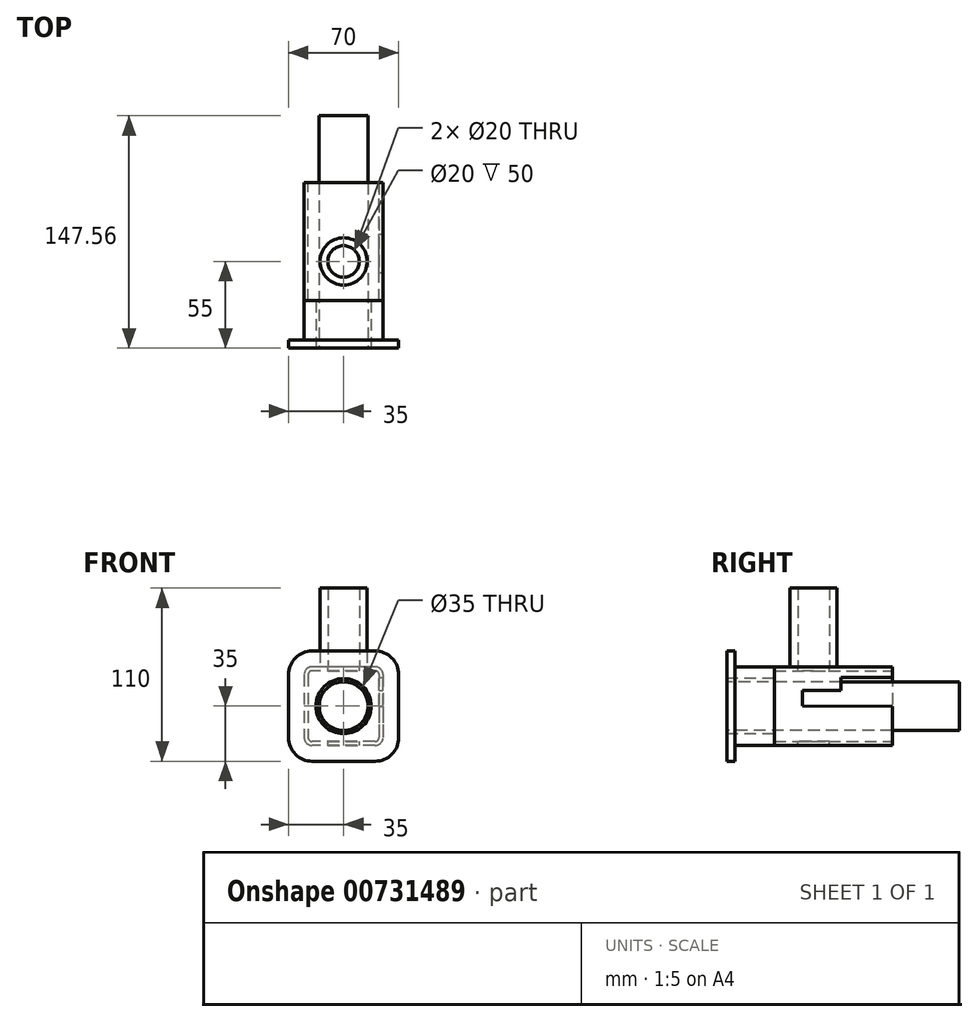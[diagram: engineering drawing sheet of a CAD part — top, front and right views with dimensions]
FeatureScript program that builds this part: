
annotation { "Feature Type Name" : "Feature", "Feature Type Description" : "" }
export const myFeature = defineFeature(function(context is Context, id is Id, definition is map)
    precondition{}
    {
        {
            var Q0;
            Q0=qCreatedBy(makeId("Front.planeOp"),FACE);
            var sketch = newSketch(context, id + "F0", { "sketchPlane" : qUnion([Q0])});
            skLineSegment(sketch, "E0.bottom", {"start": v(25, 25) * mm, "end": v(-25, 25) * mm});
            skLineSegment(sketch, "E0.top", {"start": v(25, -25) * mm, "end": v(-25, -25) * mm});
            skLineSegment(sketch, "E0.left", {"start": v(25, 25) * mm, "end": v(25, -25) * mm});
            skLineSegment(sketch, "E0.right", {"start": v(-25, 25) * mm, "end": v(-25, -25) * mm});
            skPoint(sketch, "E0.middle", {"position": v(0, 0) * mm});
            skSolve(sketch);
        }
        {
            var Q0;
            Q0 = qSketchRegion(id + "F0", true);
            extrude(context, id + "F1", {"entities" : qUnion([Q0]), "depth" : 75 * mm, "offsetDistance" : 25 * mm});
        }
        {
            var Q0;
            Q0=makeQuery(id+"F1.opExtrude","SWEPT_EDGE",EDGE,{"disambiguationData":[OSD([sQuery(id+"F0.wireOp",EDGE,"E0.top"),sQuery(id+"F0.wireOp",EDGE,"E0.right")])]});
            var Q1;
            Q1=makeQuery(id+"F1.opExtrude","SWEPT_EDGE",EDGE,{"disambiguationData":[OSD([sQuery(id+"F0.wireOp",EDGE,"E0.top"),sQuery(id+"F0.wireOp",EDGE,"E0.left")])]});
            var Q2;
            Q2=makeQuery(id+"F1.opExtrude","SWEPT_EDGE",EDGE,{"disambiguationData":[OSD([sQuery(id+"F0.wireOp",EDGE,"E0.bottom"),sQuery(id+"F0.wireOp",EDGE,"E0.right")])]});
            var Q3;
            Q3=makeQuery(id+"F1.opExtrude","SWEPT_EDGE",EDGE,{"disambiguationData":[OSD([sQuery(id+"F0.wireOp",EDGE,"E0.bottom"),sQuery(id+"F0.wireOp",EDGE,"E0.left")])]});
            fillet(context, id + "F2", {"entities" : qUnion([Q0, Q1, Q2, Q3]), "radius" : 5 * mm, "tangentPropagation" : true, "allowEdgeOverflow" : false});
        }
        {
            var Q0;
            Q0=makeQuery(id+"F1.opExtrude","CAP_FACE",FACE,{"disambiguationData":[OSD([sQuery(id+"F0.wireOp",EDGE,"E0.bottom"),sQuery(id+"F0.wireOp",EDGE,"E0.top"),sQuery(id+"F0.wireOp",EDGE,"E0.left"),sQuery(id+"F0.wireOp",EDGE,"E0.right")])],"isStart":false});
            var Q1;
            Q1=makeQuery(id+"F1.opExtrude","CAP_FACE",FACE,{"disambiguationData":[OSD([sQuery(id+"F0.wireOp",EDGE,"E0.bottom"),sQuery(id+"F0.wireOp",EDGE,"E0.top"),sQuery(id+"F0.wireOp",EDGE,"E0.left"),sQuery(id+"F0.wireOp",EDGE,"E0.right")])],"isStart":true});
            shell(context, id + "F3", {"entities" : qUnion([Q0, Q1]), "thickness" : 2.5 * mm});
        }
        {
            var Q0;
            Q0=makeQuery(id+"F1.opExtrude","SWEPT_FACE",FACE,{"disambiguationData":[OSD([sQuery(id+"F0.wireOp",EDGE,"E0.bottom")])]});
            var sketch = newSketch(context, id + "F4", { "sketchPlane" : qUnion([Q0])});
            skCircle(sketch, "E1", {"center": v(0, -50) * mm, "radius": 10 * mm});
            skSolve(sketch);
        }
        {
            var Q0;
            Q0 = qSketchRegion(id + "F4", true);
            extrude(context, id + "F5", {"entities" : qUnion([Q0]), "operationType" : NewBodyOperationType.REMOVE, "endBound" : BoundingType.THROUGH_ALL, "oppositeDirection" : true, "depth" : 41.42 * mm, "offsetDistance" : 25 * mm});
        }
        {
            var Q0;
            Q0=makeQuery(id+"F1.opExtrude","SWEPT_FACE",FACE,{"disambiguationData":[OSD([sQuery(id+"F0.wireOp",EDGE,"E0.left")])]});
            var sketch = newSketch(context, id + "F6", { "sketchPlane" : qUnion([Q0])});
            skLineSegment(sketch, "E2", {"start": v(-57, 0) * mm, "end": v(-57, 10) * mm});
            skLineSegment(sketch, "E3", {"start": v(-57, 10) * mm, "end": v(-32.57, 10) * mm});
            skLineSegment(sketch, "E4", {"start": v(-32.57, 10) * mm, "end": v(-32.57, 18.28) * mm});
            skLineSegment(sketch, "E5", {"start": v(0, 18.28) * mm, "end": v(0, -0.12) * mm});
            skLineSegment(sketch, "E6", {"start": v(0, 18.28) * mm, "end": v(-32.57, 18.28) * mm});
            skLineSegment(sketch, "E7", {"start": v(0, -0.12) * mm, "end": v(-57, 0) * mm});
            skSolve(sketch);
        }
        {
            var Q0;
            Q0=makeQuery(id+"F6.imprint","IMPRINT",FACE,{"disambiguationData":[TD([[makeQuery(id+"F6.imprint","IMPRINT",EDGE,{"derivedFrom":sQuery(id+"F6.wireOp",EDGE,"E2")}),-1.0]])]});
            extrude(context, id + "F7", {"entities" : qUnion([Q0]), "operationType" : NewBodyOperationType.REMOVE, "oppositeDirection" : true, "depth" : 3 * mm, "offsetDistance" : 25 * mm});
        }
        {
            var Q0;
            Q0=makeQuery(id+"F1.opExtrude","CAP_FACE",FACE,{"disambiguationData":[OSD([sQuery(id+"F0.wireOp",EDGE,"E0.bottom"),sQuery(id+"F0.wireOp",EDGE,"E0.top"),sQuery(id+"F0.wireOp",EDGE,"E0.left"),sQuery(id+"F0.wireOp",EDGE,"E0.right")])],"isStart":false});
            var sketch = newSketch(context, id + "F8", { "sketchPlane" : qUnion([Q0])});
            skLineSegment(sketch, "E8.0", {"start": v(20, 25) * mm, "end": v(-20, 25) * mm});
            skArc(sketch, "E9.0", {"start": v(25, 20) * mm, "mid": v(23.54, 23.54) * mm, "end": v(20, 25) * mm});
            skLineSegment(sketch, "E10.0", {"start": v(25, 20) * mm, "end": v(25, -20) * mm});
            skArc(sketch, "E11.0", {"start": v(20, -25) * mm, "mid": v(23.54, -23.54) * mm, "end": v(25, -20) * mm});
            skLineSegment(sketch, "E12.0", {"start": v(20, -25) * mm, "end": v(-20, -25) * mm});
            skArc(sketch, "E13.0", {"start": v(-25, -20) * mm, "mid": v(-23.54, -23.54) * mm, "end": v(-20, -25) * mm});
            skLineSegment(sketch, "E14.0", {"start": v(-25, 20) * mm, "end": v(-25, -20) * mm});
            skArc(sketch, "E15.0", {"start": v(-20, 25) * mm, "mid": v(-23.54, 23.54) * mm, "end": v(-25, 20) * mm});
            skSolve(sketch);
        }
        {
            var Q0;
            Q0 = qSketchRegion(id + "F8", true);
            extrude(context, id + "F9", {"entities" : qUnion([Q0]), "depth" : 25 * mm, "offsetDistance" : 25 * mm});
        }
        {
            var Q0;
            Q0=makeQuery(id+"F9.opExtrude","CAP_FACE",FACE,{"disambiguationData":[OSD([sQuery(id+"F8.wireOp",EDGE,"E8.0"),sQuery(id+"F8.wireOp",EDGE,"E9.0"),sQuery(id+"F8.wireOp",EDGE,"E10.0"),sQuery(id+"F8.wireOp",EDGE,"E11.0"),sQuery(id+"F8.wireOp",EDGE,"E12.0"),sQuery(id+"F8.wireOp",EDGE,"E13.0"),sQuery(id+"F8.wireOp",EDGE,"E14.0"),sQuery(id+"F8.wireOp",EDGE,"E15.0")])],"isStart":false});
            var sketch = newSketch(context, id + "F10", { "sketchPlane" : qUnion([Q0])});
            skArc(sketch, "E16.0", {"start": v(35, 20) * mm, "mid": v(30.6, 30.6) * mm, "end": v(20, 35) * mm});
            skLineSegment(sketch, "E16.1", {"start": v(35, 20) * mm, "end": v(35, -20) * mm});
            skLineSegment(sketch, "E16.2", {"start": v(20, 35) * mm, "end": v(-20, 35) * mm});
            skArc(sketch, "E16.3", {"start": v(20, -35) * mm, "mid": v(30.6, -30.6) * mm, "end": v(35, -20) * mm});
            skArc(sketch, "E16.4", {"start": v(-20, 35) * mm, "mid": v(-30.6, 30.6) * mm, "end": v(-35, 20) * mm});
            skLineSegment(sketch, "E16.5", {"start": v(-35, 20) * mm, "end": v(-35, -20) * mm});
            skArc(sketch, "E16.6", {"start": v(-35, -20) * mm, "mid": v(-30.6, -30.6) * mm, "end": v(-20, -35) * mm});
            skLineSegment(sketch, "E16.7", {"start": v(20, -35) * mm, "end": v(-20, -35) * mm});
            skSolve(sketch);
        }
        {
            var Q0;
            Q0 = qSketchRegion(id + "F10", true);
            extrude(context, id + "F11", {"entities" : qUnion([Q0]), "operationType" : NewBodyOperationType.ADD, "depth" : 5 * mm, "offsetDistance" : 25 * mm});
        }
        {
            var Q0;
            Q0=makeQuery(id+"F11.opExtrude","CAP_FACE",FACE,{"disambiguationData":[OSD([sQuery(id+"F10.wireOp",EDGE,"E16.0"),sQuery(id+"F10.wireOp",EDGE,"E16.1"),sQuery(id+"F10.wireOp",EDGE,"E16.2"),sQuery(id+"F10.wireOp",EDGE,"E16.3"),sQuery(id+"F10.wireOp",EDGE,"E16.4"),sQuery(id+"F10.wireOp",EDGE,"E16.5"),sQuery(id+"F10.wireOp",EDGE,"E16.6"),sQuery(id+"F10.wireOp",EDGE,"E16.7")])],"isStart":false});
            var sketch = newSketch(context, id + "F12", { "sketchPlane" : qUnion([Q0])});
            skCircle(sketch, "E17", {"center": v(0, 0) * mm, "radius": 17.5 * mm});
            skSolve(sketch);
        }
        {
            var Q0;
            Q0 = qSketchRegion(id + "F12", true);
            extrude(context, id + "F13", {"entities" : qUnion([Q0]), "operationType" : NewBodyOperationType.REMOVE, "endBound" : BoundingType.THROUGH_ALL, "oppositeDirection" : true, "depth" : 25 * mm, "offsetDistance" : 25 * mm});
        }
        {
            var Q0;
            Q0=makeQuery(id+"F11.opExtrude","CAP_FACE",FACE,{"disambiguationData":[OSD([sQuery(id+"F10.wireOp",EDGE,"E16.0"),sQuery(id+"F10.wireOp",EDGE,"E16.1"),sQuery(id+"F10.wireOp",EDGE,"E16.2"),sQuery(id+"F10.wireOp",EDGE,"E16.3"),sQuery(id+"F10.wireOp",EDGE,"E16.4"),sQuery(id+"F10.wireOp",EDGE,"E16.5"),sQuery(id+"F10.wireOp",EDGE,"E16.6"),sQuery(id+"F10.wireOp",EDGE,"E16.7")])],"isStart":false});
            var sketch = newSketch(context, id + "F14", { "sketchPlane" : qUnion([Q0])});
            skCircle(sketch, "E18.0", {"center": v(0, 0) * mm, "radius": 17.5 * mm});
            skCircle(sketch, "E19.0", {"center": v(0, 0) * mm, "radius": 15.5 * mm});
            skSolve(sketch);
        }
        {
            var Q0;
            Q0=makeQuery(id+"F14.imprint","IMPRINT",FACE,{"disambiguationData":[TD([[makeQuery(id+"F14.imprint","IMPRINT",EDGE,{"derivedFrom":sQuery(id+"F14.wireOp",EDGE,"E19.0")}),1.0]])]});
            var Q1;
            Q1=sQuery(id+"F14.wireOp",EDGE,"E19.0");
            extrude(context, id + "F15", {"entities" : qUnion([Q0]), "surfaceEntities" : qUnion([Q1]), "oppositeDirection" : true, "depth" : 147.56 * mm, "offsetDistance" : 25 * mm});
        }
        {
            var Q0;
            Q0=makeQuery(id+"F1.opExtrude","SWEPT_FACE",FACE,{"disambiguationData":[OSD([sQuery(id+"F0.wireOp",EDGE,"E0.bottom")])]});
            var sketch = newSketch(context, id + "F16", { "sketchPlane" : qUnion([Q0])});
            skCircle(sketch, "E20.0", {"center": v(0, -50) * mm, "radius": 10 * mm});
            skCircle(sketch, "E21", {"center": v(0, -50) * mm, "radius": 15 * mm});
            skSolve(sketch);
        }
        {
            var Q0;
            Q0=makeQuery(id+"F16.imprint","IMPRINT",FACE,{"disambiguationData":[TD([[makeQuery(id+"F16.imprint","IMPRINT",EDGE,{"derivedFrom":sQuery(id+"F16.wireOp",EDGE,"E20.0")}),-1.0]])]});
            extrude(context, id + "F17", {"entities" : qUnion([Q0]), "depth" : 50 * mm, "offsetDistance" : 25 * mm});
        }
    });
